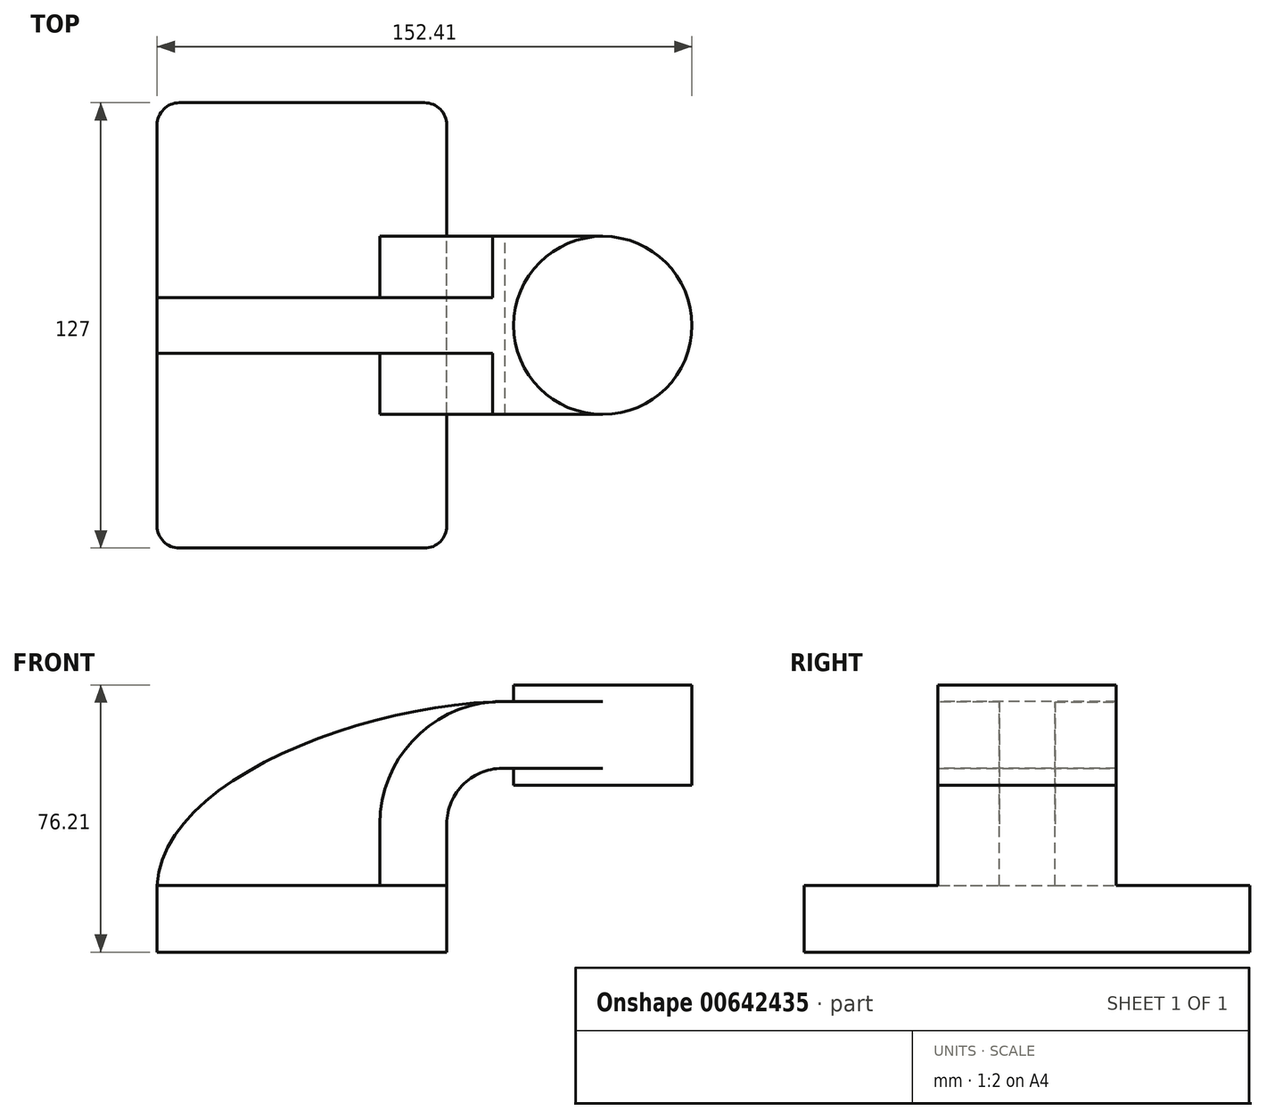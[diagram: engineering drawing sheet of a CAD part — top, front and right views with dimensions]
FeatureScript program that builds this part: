
annotation { "Feature Type Name" : "Feature", "Feature Type Description" : "" }
export const myFeature = defineFeature(function(context is Context, id is Id, definition is map)
    precondition{}
    {
        {
            var Q0;
            Q0=qCreatedBy(makeId("Front.planeOp"),FACE);
            var sketch = newSketch(context, id + "F0", { "sketchPlane" : qUnion([Q0])});
            skLineSegment(sketch, "E0.bottom", {"start": v(-41.28, 9.52) * mm, "end": v(41.28, 9.53) * mm});
            skLineSegment(sketch, "E0.top", {"start": v(-41.28, -9.53) * mm, "end": v(41.28, -9.53) * mm});
            skLineSegment(sketch, "E0.left", {"start": v(-41.28, 9.52) * mm, "end": v(-41.27, -9.53) * mm});
            skLineSegment(sketch, "E0.right", {"start": v(41.28, 9.53) * mm, "end": v(41.28, -9.52) * mm});
            skPoint(sketch, "E0.middle", {"position": v(0, 0) * mm});
            skLineSegment(sketch, "E1.bottom", {"start": v(111.12, 38.1) * mm, "end": v(60.32, 38.1) * mm});
            skLineSegment(sketch, "E1.top", {"start": v(111.12, 66.68) * mm, "end": v(60.32, 66.68) * mm});
            skLineSegment(sketch, "E1.left", {"start": v(111.13, 38.1) * mm, "end": v(111.12, 66.68) * mm});
            skLineSegment(sketch, "E1.right", {"start": v(60.32, 38.1) * mm, "end": v(60.32, 66.68) * mm});
            skPoint(sketch, "E1.middle", {"position": v(85.72, 52.39) * mm});
            skLineSegment(sketch, "E2", {"start": v(41.27, 9.53) * mm, "end": v(41.27, 27.02) * mm});
            skArc(sketch, "E3", {"start": v(41.27, 27.02) * mm, "mid": v(46.18, 38.5) * mm, "end": v(57.87, 42.88) * mm});
            skLineSegment(sketch, "E4", {"start": v(57.87, 42.88) * mm, "end": v(85.72, 42.88) * mm});
            skLineSegment(sketch, "E5.0", {"start": v(58.22, 61.93) * mm, "end": v(85.72, 61.93) * mm});
            skArc(sketch, "E5.1", {"start": v(22.23, 27.02) * mm, "mid": v(32.84, 52.09) * mm, "end": v(58.22, 61.93) * mm});
            skLineSegment(sketch, "E5.2", {"start": v(22.22, 9.53) * mm, "end": v(22.22, 27.02) * mm});
            skFitSpline(sketch, "E6", {"points": [v(-41.28, 9.53) * mm, v(58.22, 61.93) * mm], "startDerivative": vector(3.24, 89.18) * mm, "endDerivative": vector(121.9, 1.13) * mm});
            skLineSegment(sketch, "E7", {"start": v(85.72, 61.93) * mm, "end": v(85.72, 42.88) * mm});
            skLineSegment(sketch, "E8", {"start": v(85.72, 66.68) * mm, "end": v(85.72, 38.1) * mm});
            skSolve(sketch);
        }
        {
            var Q0;
            Q0=makeQuery(id+"F0.imprint","IMPRINT",FACE,{"disambiguationData":[TD([[makeQuery(id+"F0.imprint","IMPRINT",EDGE,{"derivedFrom":sQuery(id+"F0.wireOp",EDGE,"E0.top")}),1.0]])]});
            extrude(context, id + "F1", {"entities" : qUnion([Q0]), "endBound" : BoundingType.SYMMETRIC, "depth" : 127 * mm, "offsetDistance" : 25.4 * mm});
        }
        {
            var Q0;
            {var subQ5=sQuery(id+"F0.wireOp",EDGE,"E7");Q0=makeQuery(id+"F0.imprint","IMPRINT",FACE,{"disambiguationData":[TD([[makeQuery(id+"F0.imprint","IMPRINT",EDGE,{"derivedFrom":subQ5}),-1.0]])]});}
            var Q1;
            {var subQ1=sQuery(id+"F0.wireOp",EDGE,"E2");Q1=makeQuery(id+"F0.imprint","IMPRINT",FACE,{"disambiguationData":[TD([[makeQuery(id+"F0.imprint","IMPRINT",EDGE,{"derivedFrom":subQ1}),1.0]])]});}
            extrude(context, id + "F2", {"entities" : qUnion([Q0, Q1]), "operationType" : NewBodyOperationType.ADD, "endBound" : BoundingType.SYMMETRIC, "depth" : 50.8 * mm, "offsetDistance" : 25.4 * mm});
        }
        {
            var Q0;
            {var subQ3=sQuery(id+"F0.wireOp",EDGE,"E5.2");Q0=makeQuery(id+"F0.imprint","IMPRINT",FACE,{"disambiguationData":[TD([[makeQuery(id+"F0.imprint","IMPRINT",EDGE,{"derivedFrom":subQ3}),1.0]])]});}
            extrude(context, id + "F3", {"entities" : qUnion([Q0]), "operationType" : NewBodyOperationType.ADD, "endBound" : BoundingType.SYMMETRIC, "depth" : 15.88 * mm, "offsetDistance" : 25.4 * mm});
        }
        {
            var Q0;
            {var subQ0=sQuery(id+"F0.wireOp",EDGE,"E4");var subQ1=sQuery(id+"F0.wireOp",EDGE,"E1.right");var subQ2=makeQuery(id+"F0.imprint","INTERSECT",VERTEX,{"derivedFrom":[subQ1,subQ0]});Q0=makeQuery(id+"F0.imprint","IMPRINT",FACE,{"disambiguationData":[TD([[makeQuery(id+"F0.imprint","IMPRINT",EDGE,{"disambiguationData":[TD([[subQ2,-1.0]])],"derivedFrom":subQ1}),-1.0]])]});}
            extrude(context, id + "F4", {"entities" : qUnion([Q0]), "operationType" : NewBodyOperationType.ADD, "endBound" : BoundingType.SYMMETRIC, "depth" : 50.8 * mm, "offsetDistance" : 25.4 * mm});
        }
        {
            var Q0;
            {var subQ4=sQuery(id+"F0.wireOp",EDGE,"E1.left");Q0=makeQuery(id+"F0.imprint","IMPRINT",FACE,{"disambiguationData":[TD([[makeQuery(id+"F0.imprint","IMPRINT",EDGE,{"derivedFrom":subQ4}),1.0]])]});}
            var Q1;
            Q1=sQuery(id+"F0.wireOp",EDGE,"E8");
            revolve(context, id + "F5", {"operationType" : NewBodyOperationType.ADD, "entities" : qUnion([Q0]), "axis" : qUnion([Q1]), "revolveType" : RevolveType.FULL});
        }
        {
            var Q0;
            Q0=makeQuery(id+"F1.opExtrude","CAP_EDGE",EDGE,{"disambiguationData":[OSD([sQuery(id+"F0.wireOp",EDGE,"E0.left")])],"isStart":false});
            var Q1;
            Q1=makeQuery(id+"F1.opExtrude","CAP_EDGE",EDGE,{"disambiguationData":[OSD([sQuery(id+"F0.wireOp",EDGE,"E0.right")])],"isStart":false});
            var Q2;
            Q2=makeQuery(id+"F1.opExtrude","CAP_EDGE",EDGE,{"disambiguationData":[OSD([sQuery(id+"F0.wireOp",EDGE,"E0.right")])],"isStart":true});
            var Q3;
            Q3=makeQuery(id+"F1.opExtrude","CAP_EDGE",EDGE,{"disambiguationData":[OSD([sQuery(id+"F0.wireOp",EDGE,"E0.left")])],"isStart":true});
            fillet(context, id + "F6", {"entities" : qUnion([Q0, Q1, Q2, Q3]), "radius" : 6.35 * mm, "tangentPropagation" : true, "allowEdgeOverflow" : false});
        }
    });
